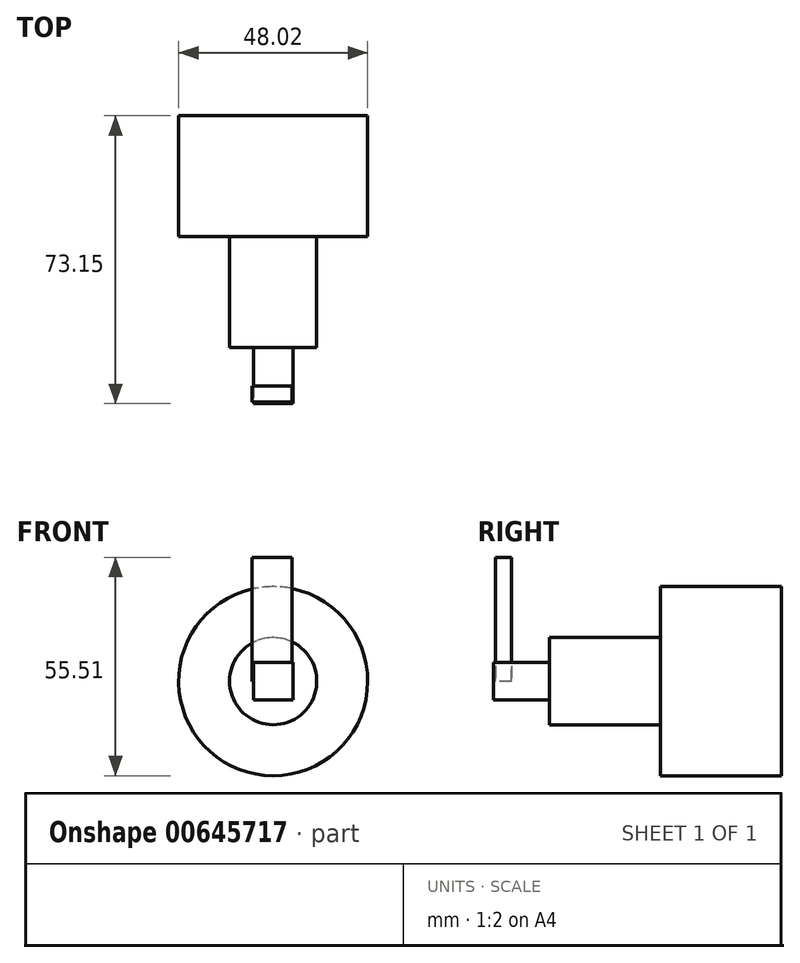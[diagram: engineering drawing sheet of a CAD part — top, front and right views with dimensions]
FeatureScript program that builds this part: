
annotation { "Feature Type Name" : "Feature", "Feature Type Description" : "" }
export const myFeature = defineFeature(function(context is Context, id is Id, definition is map)
    precondition{}
    {
        {
            var Q0;
            Q0=qCreatedBy(makeId("Front.planeOp"),FACE);
            var sketch = newSketch(context, id + "F0", { "sketchPlane" : qUnion([Q0])});
            skCircle(sketch, "E0", {"center": v(0, 0) * mm, "radius": 24.01 * mm});
            skSolve(sketch);
        }
        {
            var Q0;
            Q0=makeQuery(id+"F0.imprint","IMPRINT",FACE,{"disambiguationData":[TD([[makeQuery(id+"F0.imprint","IMPRINT",EDGE,{"derivedFrom":sQuery(id+"F0.wireOp",EDGE,"E0")}),1.0]])]});
            extrude(context, id + "F1", {"entities" : qUnion([Q0]), "depth" : 30.73 * mm, "offsetDistance" : 25.4 * mm});
        }
        {
            var Q0;
            Q0=qCreatedBy(makeId("Front.planeOp"),FACE);
            var sketch = newSketch(context, id + "F2", { "sketchPlane" : qUnion([Q0])});
            skCircle(sketch, "E1", {"center": v(0, 0) * mm, "radius": 11.07 * mm});
            skSolve(sketch);
        }
        {
            var Q0;
            Q0=makeQuery(id+"F2.imprint","IMPRINT",FACE,{"disambiguationData":[TD([[makeQuery(id+"F2.imprint","IMPRINT",EDGE,{"derivedFrom":sQuery(id+"F2.wireOp",EDGE,"E1")}),1.0]])]});
            extrude(context, id + "F3", {"entities" : qUnion([Q0]), "operationType" : NewBodyOperationType.ADD, "depth" : 58.93 * mm, "offsetDistance" : 25.4 * mm});
        }
        {
            var Q0;
            Q0=qCreatedBy(makeId("Front.planeOp"),FACE);
            var sketch = newSketch(context, id + "F4", { "sketchPlane" : qUnion([Q0])});
            skLineSegment(sketch, "E2.bottom", {"start": v(-5.04, 4.75) * mm, "end": v(5.04, 4.75) * mm});
            skLineSegment(sketch, "E2.top", {"start": v(-5.04, -4.75) * mm, "end": v(5.04, -4.75) * mm});
            skLineSegment(sketch, "E2.left", {"start": v(-5.04, 4.75) * mm, "end": v(-5.04, -4.75) * mm});
            skLineSegment(sketch, "E2.right", {"start": v(5.04, 4.75) * mm, "end": v(5.04, -4.75) * mm});
            skSolve(sketch);
        }
        {
            var Q0;
            Q0 = qSketchRegion(id + "F4", true);
            extrude(context, id + "F5", {"entities" : qUnion([Q0]), "operationType" : NewBodyOperationType.ADD, "depth" : 73.15 * mm, "offsetDistance" : 25.4 * mm});
        }
        {
            var Q0;
            Q0=qCreatedBy(makeId("Top.planeOp"),FACE);
            var sketch = newSketch(context, id + "F6", { "sketchPlane" : qUnion([Q0])});
            skLineSegment(sketch, "E3.bottom", {"start": v(-5.32, -68.64) * mm, "end": v(4.75, -68.64) * mm});
            skLineSegment(sketch, "E3.top", {"start": v(-5.32, -72.67) * mm, "end": v(4.75, -72.67) * mm});
            skLineSegment(sketch, "E3.left", {"start": v(-5.32, -68.64) * mm, "end": v(-5.32, -72.67) * mm});
            skLineSegment(sketch, "E3.right", {"start": v(4.75, -68.64) * mm, "end": v(4.75, -72.67) * mm});
            skSolve(sketch);
        }
        {
            var Q0;
            Q0 = qSketchRegion(id + "F6", true);
            extrude(context, id + "F7", {"entities" : qUnion([Q0]), "operationType" : NewBodyOperationType.ADD, "depth" : 31.5 * mm, "offsetDistance" : 25.4 * mm});
        }
    });
